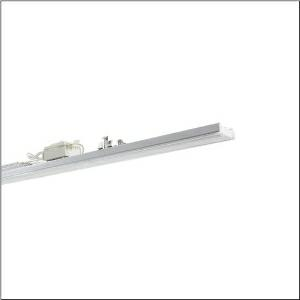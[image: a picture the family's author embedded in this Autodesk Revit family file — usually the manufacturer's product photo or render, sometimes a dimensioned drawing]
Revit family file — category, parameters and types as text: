
# Revit family: licross_11_recessed_ho_51te1edv4m5s
name_source: partatom
category: Lighting Fixtures
units: mm (PartAtom-declared; Revit-internal decimal feet)

## family parameters
Cut with Voids When Loaded = No
Host = Face
Light Source = No
Part Type = Normal
Room Calculation Point = No
Round Connector Dimension = Use Diameter
Shared = No

## types (1)
- --- (1 x LED, 25560 lm, 144.7 W, 4000K)
    Apparent Load = 145 VA
    CIE Flux Codes = 85 95 99 100 100
    Color Rendering = 80
    Color Temperature = 4000K
    Default Elevation = 1800 mm
    Description = Licross 11 Recessed HO, luminaire insert, of sheet steel, galvanised, coil coated, white, length: 2.250mm, width: 66mm, height: 67mm, LED rated luminous flux: 25.560lm, light colour: 840, SDCM (Standard Deviation of Colour Matching)MacAdam ≤ 2 SDCM (initial), control gear: DALI 2, with plug, 5-pole, with phase selection, mains connection: 220..240V, AC, 50/60Hz, rated input power: 145W, internal wiring halogen-free, primary light control with lens, of plastic, primary optical cover: cover, of PMMA, light emission: direct distribution, primary light characteristic: symmetric, protection rating (complete): IP54, insulation class (complete): insulation class I (protective earthing), certification: CE, ENEC, VDE, UKCA, protection symbol: D if used in an environment with non-conductive dust loads with corresponding accessories, impact resistance: IK06, permissible ambient temperature for indoor applications: -40..+35°C, corresponds to IFS (International Featured Standards) requirements for safety and quality in the food industry, reducing of maximum allowable ambient temperature of 5°C with ceiling mounting, LABS conformity tested according to VDMA 24364:2018-05, The light source and the operating device comply with the requirements of the Ecodesign Regulation (EU) 2019/2020 and are replaceable in accordance with this regulation, packaging unit: 1 piece
    Height = 58 mm
    Lamp = 1 x LED
    Lamp Light Flux = 25560 lm
    Lamp Power = 144.7 W
    Lamp count = 1
    Length = 2250 mm
    Luminous efficacy = 177 lm/W
    Manufacturer = Siteco
    ModVariant = No
    Model = 51TE1EDV4M5S
    Mounting Place = Ceiling
    Mounting Type = Pendant
    Number of Poles = 1
    OnlyDefault = Yes
    Power Factor = 1
    Product Name = Licross 11 Recessed HO
    Product group = luminaire insert | ceiling pendant
    ProductGroupID = 901
    Protection Class = Protection class I
    Protection Degree = IP 54
    RLX_Detail_Level = 1
    RLX_Emergency_Light_Flux = 0 lm
    RLX_Emergency_Type = 0
    RLX_Emergency_Type_DB = No
    RlxData = <blob elided: 29973 chars, md5=5af2b971>
    Socket = socket
    Standby Power = 0 W
    System Light Flux = 25560 lm
    System Power = 145 W
    Type Comments = factory setting: luminous flux: 100 % | dim-lin: 254 | 665 mA
    Type Image = l_1296930.jpg
    URL = http://relux.com
    VarID = @adj_099603
    Voltage = 0 V
    Weight = 0.00 kg
    Width = 66 mm

## geometry (parser evidence)
native form markers: Blend x4, Sweep x9
no freeform markers — native parametric forms only
